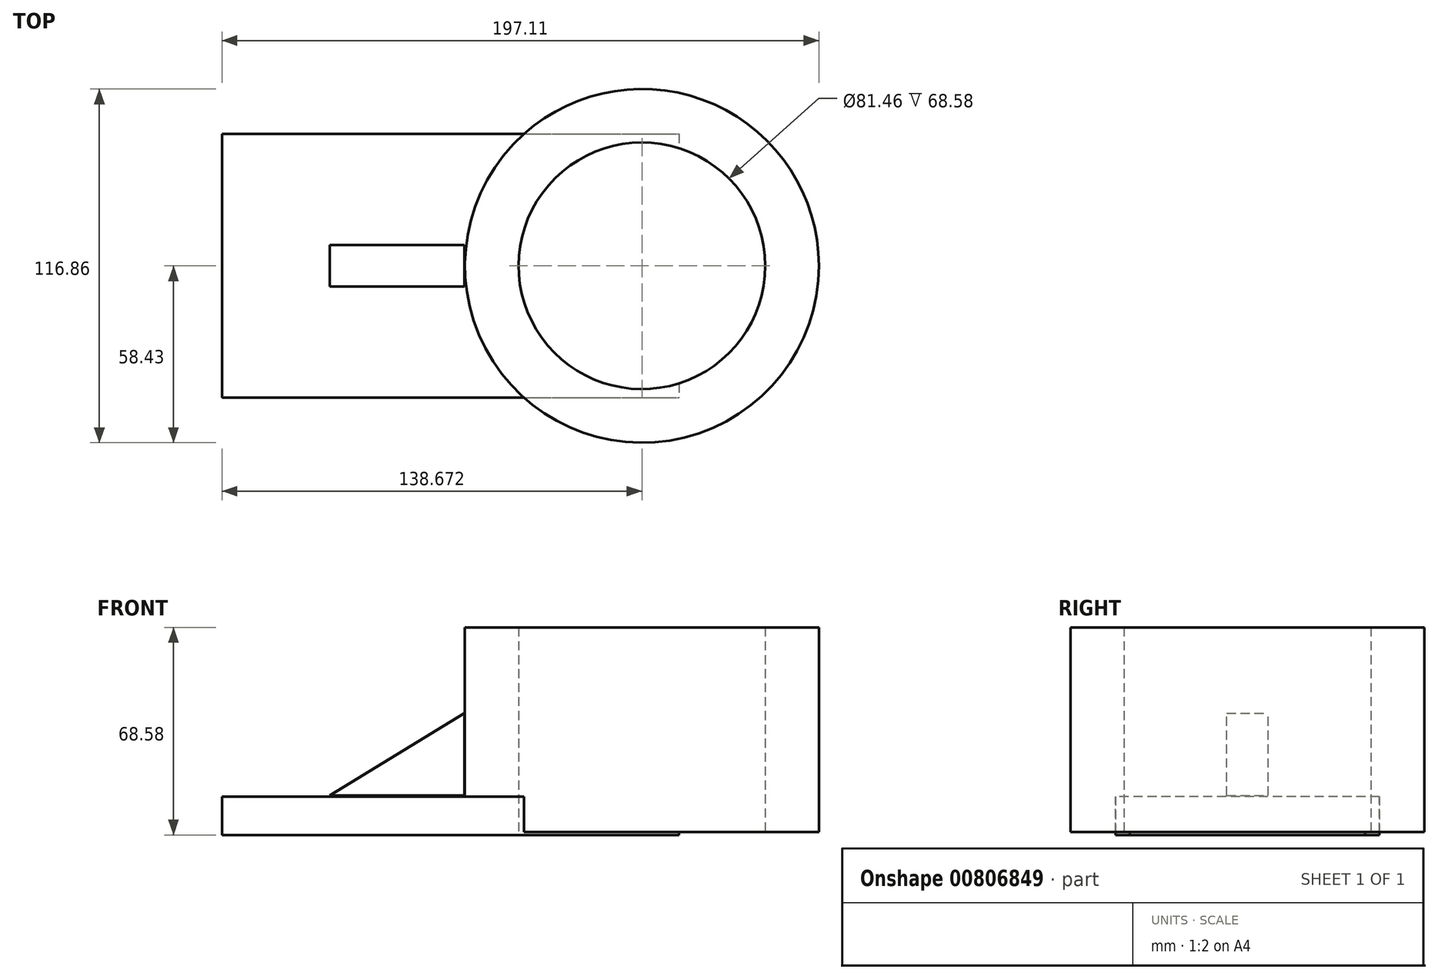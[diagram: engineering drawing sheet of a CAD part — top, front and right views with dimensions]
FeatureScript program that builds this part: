
annotation { "Feature Type Name" : "Feature", "Feature Type Description" : "" }
export const myFeature = defineFeature(function(context is Context, id is Id, definition is map)
    precondition{}
    {
        {
            var Q0;
            Q0=qCreatedBy(makeId("Top.planeOp"),FACE);
            var sketch = newSketch(context, id + "F0", { "sketchPlane" : qUnion([Q0])});
            skLineSegment(sketch, "E0.bottom", {"start": v(-75.49, 43.59) * mm, "end": v(75.49, 43.59) * mm});
            skLineSegment(sketch, "E0.top", {"start": v(-75.49, -43.59) * mm, "end": v(75.49, -43.59) * mm});
            skLineSegment(sketch, "E0.left", {"start": v(-75.49, 43.59) * mm, "end": v(-75.49, -43.59) * mm});
            skLineSegment(sketch, "E0.right", {"start": v(75.49, 43.59) * mm, "end": v(75.49, -43.59) * mm});
            skPoint(sketch, "E0.middle", {"position": v(0, 0) * mm});
            skSolve(sketch);
        }
        {
            var Q0;
            Q0 = qSketchRegion(id + "F0", true);
            extrude(context, id + "F1", {"entities" : qUnion([Q0]), "depth" : 12.7 * mm, "offsetDistance" : 25.4 * mm});
        }
        {
            var Q0;
            Q0=makeQuery(id+"F1.opExtrude","CAP_FACE",FACE,{"disambiguationData":[OSD([sQuery(id+"F0.wireOp",EDGE,"E0.bottom"),sQuery(id+"F0.wireOp",EDGE,"E0.top"),sQuery(id+"F0.wireOp",EDGE,"E0.left"),sQuery(id+"F0.wireOp",EDGE,"E0.right")])],"isStart":false});
            var sketch = newSketch(context, id + "F2", { "sketchPlane" : qUnion([Q0])});
            skLineSegment(sketch, "E1", {"start": v(0, 0) * mm, "end": v(63.18, 0) * mm});
            skCircle(sketch, "E2", {"center": v(63.18, 0) * mm, "radius": 58.43 * mm});
            skCircle(sketch, "E3", {"center": v(63.18, 0) * mm, "radius": 40.73 * mm});
            skSolve(sketch);
        }
        {
            var Q0;
            {var subQ3=sQuery(id+"F2.wireOp",EDGE,"E2");var subQ6=sQuery(id+"F2.wireOp",EDGE,"E1");var subQ9=makeQuery(id+"F2.imprint","INTERSECT",VERTEX,{"derivedFrom":[subQ6,subQ3]});Q0=makeQuery(id+"F2.imprint","IMPRINT",FACE,{"disambiguationData":[TD([[makeQuery(id+"F2.imprint","IMPRINT",EDGE,{"disambiguationData":[TD([[subQ9,-1.0]])],"derivedFrom":subQ6}),1.0]])]});}
            var Q1;
            {var subQ3=sQuery(id+"F2.wireOp",EDGE,"E2");var subQ5=sQuery(id+"F2.wireOp",EDGE,"E1");var subQ6=makeQuery(id+"F2.imprint","INTERSECT",VERTEX,{"derivedFrom":[subQ5,subQ3]});Q1=makeQuery(id+"F2.imprint","IMPRINT",FACE,{"disambiguationData":[TD([[makeQuery(id+"F2.imprint","IMPRINT",EDGE,{"disambiguationData":[TD([[subQ6,-1.0]])],"derivedFrom":subQ5}),-1.0]])]});}
            var Q2;
            {var subQ1=makeQuery(id+"F1.opExtrude","CAP_EDGE",EDGE,{"disambiguationData":[OSD([sQuery(id+"F0.wireOp",EDGE,"E0.bottom")])],"isStart":false});var subQ3=sQuery(id+"F2.wireOp",EDGE,"E2");var subQ4=makeQuery(id+"F2.imprint","INTERSECT",VERTEX,{"derivedFrom":[subQ1,subQ3]});Q2=makeQuery(id+"F2.imprint","IMPRINT",FACE,{"disambiguationData":[TD([[makeQuery(id+"F2.imprint","IMPRINT",EDGE,{"disambiguationData":[TD([[subQ4,1.0]])],"derivedFrom":subQ3}),1.0]])]});}
            extrude(context, id + "F3", {"entities" : qUnion([Q0, Q1, Q2]), "operationType" : NewBodyOperationType.ADD, "depth" : 55.88 * mm, "offsetDistance" : 25.4 * mm});
        }
        {
            var Q0;
            {var subQ0=sQuery(id+"F0.wireOp",EDGE,"E0.right");Q0=makeQuery(id+"F3.boolean.opBoolean","SPLIT",FACE,{"disambiguationData":[TD([makeQuery(id+"F1.opExtrude","SWEPT_FACE",FACE,{"disambiguationData":[OSD([subQ0])]})])],"derivedFrom":makeQuery(id+"F1.opExtrude","CAP_FACE",FACE,{"disambiguationData":[OSD([sQuery(id+"F0.wireOp",EDGE,"E0.bottom"),sQuery(id+"F0.wireOp",EDGE,"E0.top"),sQuery(id+"F0.wireOp",EDGE,"E0.left"),subQ0])],"isStart":false})});}
            extrude(context, id + "F4", {"entities" : qUnion([Q0]), "operationType" : NewBodyOperationType.REMOVE, "oppositeDirection" : true, "depth" : 452.12 * mm, "offsetDistance" : 25.4 * mm});
        }
        {
            var Q0;
            Q0=makeQuery(id+"F3.opExtrude","CAP_FACE",FACE,{"disambiguationData":[OSD([sQuery(id+"F2.wireOp",EDGE,"E2"),sQuery(id+"F2.wireOp",EDGE,"E3")])],"isStart":true});
            extrude(context, id + "F5", {"entities" : qUnion([Q0]), "operationType" : NewBodyOperationType.ADD, "depth" : 11.68 * mm, "offsetDistance" : 25.4 * mm});
        }
        {
            var Q0;
            Q0=qCreatedBy(makeId("Front.planeOp"),FACE);
            var sketch = newSketch(context, id + "F6", { "sketchPlane" : qUnion([Q0])});
            skLineSegment(sketch, "E4", {"start": v(4.62, 40.2) * mm, "end": v(-39.84, 13.06) * mm});
            skLineSegment(sketch, "E5", {"start": v(-39.84, 13.06) * mm, "end": v(4.62, 13.06) * mm});
            skLineSegment(sketch, "E6", {"start": v(4.62, 13.06) * mm, "end": v(4.62, 40.2) * mm});
            skSolve(sketch);
        }
        {
            var Q0;
            Q0 = qSketchRegion(id + "F6", true);
            extrude(context, id + "F7", {"entities" : qUnion([Q0]), "endBound" : BoundingType.SYMMETRIC, "depth" : 13.72 * mm, "offsetDistance" : 25.4 * mm});
        }
    });
